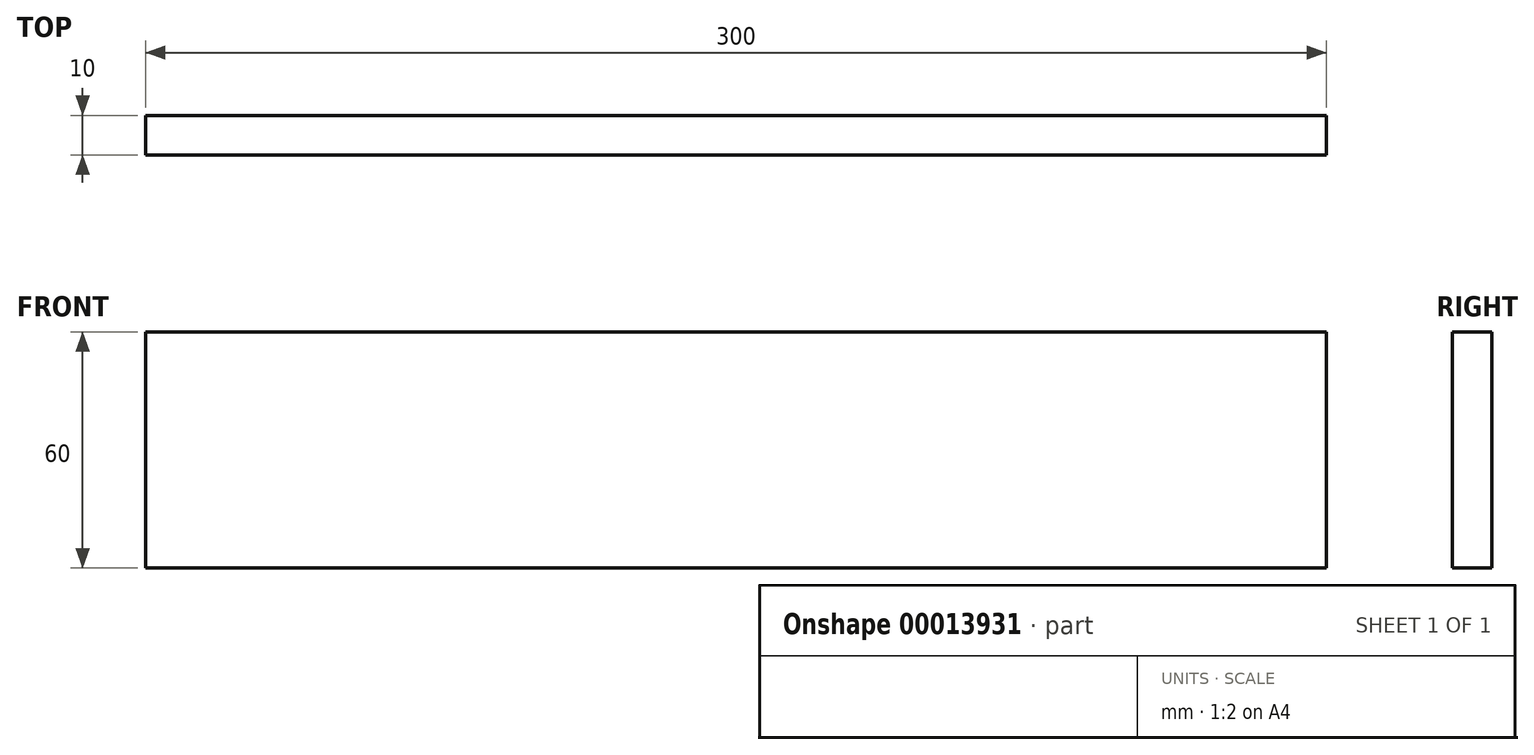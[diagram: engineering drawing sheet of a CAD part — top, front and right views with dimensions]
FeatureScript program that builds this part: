
annotation { "Feature Type Name" : "Feature", "Feature Type Description" : "" }
export const myFeature = defineFeature(function(context is Context, id is Id, definition is map)
    precondition{}
    {
        {
            var Q0;
            Q0=qCreatedBy(makeId("Front.planeOp"),FACE);
            var sketch = newSketch(context, id + "F0", { "sketchPlane" : qUnion([Q0])});
            skLineSegment(sketch, "E0.bottom", {"start": v(-194.2, -15.15) * mm, "end": v(105.8, -15.15) * mm});
            skLineSegment(sketch, "E0.top", {"start": v(-194.2, -75.15) * mm, "end": v(105.8, -75.15) * mm});
            skLineSegment(sketch, "E0.left", {"start": v(-194.2, -15.15) * mm, "end": v(-194.2, -75.15) * mm});
            skLineSegment(sketch, "E0.right", {"start": v(105.8, -15.15) * mm, "end": v(105.8, -75.15) * mm});
            skSolve(sketch);
        }
        {
            var Q0;
            Q0=makeQuery(id+"F0.imprint","IMPRINT",FACE,{"disambiguationData":[TD([[makeQuery(id+"F0.imprint","IMPRINT",EDGE,{"derivedFrom":sQuery(id+"F0.wireOp",EDGE,"E0.bottom")}),-1.0]])]});
            extrude(context, id + "F1", {"entities" : qUnion([Q0]), "depth" : 10 * mm});
        }
    });
